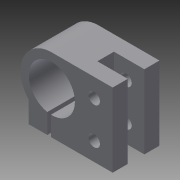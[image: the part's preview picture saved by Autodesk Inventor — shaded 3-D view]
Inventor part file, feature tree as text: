
AUTODESK INVENTOR PART (.ipt)
format: ipt  version: 2015 (Build 190159000, 159)  size: 123,392 bytes
history: native  units: mm
features: extrude x2, sketch x2
ambient origin geometry x8: Origin, YZ Plane, XZ Plane, XY Plane, X Axis, Y Axis, Z Axis, Center Point
bodies: Solid1 (feature_tree)
feature tree (4):
  extrude  "Extrusion1"  Depth=25.4mm TaperAngle=0.0deg
  extrude  "Extrusion2"  [1 undecoded]
  sketch  "Sketch1"  dims[d0=50.0mm d1=40.0mm d2=10.0mm d3=10.0mm d4=20.0mm d5=6.2mm d6=6.2mm d7=45.5mm d8=35.5mm d9=4.5mm d10=4.5mm d11=12.5mm d12=12.5mm d13=2.0mm d14=25.4mm d15=0.0mm]
  sketch  "Sketch2"  dims[d16=8.2mm d17=16.5mm d18=9.0mm d19=25.4mm d20=0.0mm]
note: 1 required parameter value undecoded (feature->parameter linkage not recoverable at this tier; creation-order binding heuristic only, values carry confidence <= 0.55)
